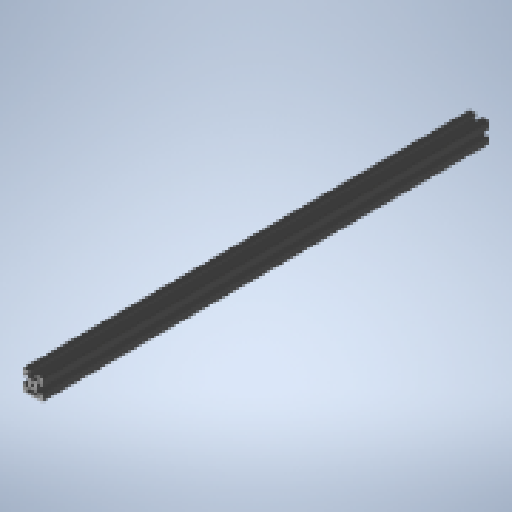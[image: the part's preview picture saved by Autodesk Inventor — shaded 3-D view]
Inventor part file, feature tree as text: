
AUTODESK INVENTOR PART (.ipt)
format: ipt  version: 2024 (Build 280153000, 153)  size: 376,832 bytes
history: native  units: mm
features: other x7, thread x2, sketch x2, extrude x1, hole x1
ambient origin geometry x8: Origin, YZ Plane, XZ Plane, XY Plane, X Axis, Y Axis, Z Axis, Center Point
bodies: Solid1 (feature_tree)
feature tree (13):
  extrude  "Extrusion1"  TaperAngle=0.0deg  [1 undecoded]
  hole  "Hole1"  [1 undecoded]
  other  "C1_XY"
  other  "C1_YZ"
  other  "C1_ZX"
  other  "C1_X"
  other  "C1_Y"
  other  "C1_Z"
  other  "C1_Center"
  thread  "Thread1"  [1 undecoded]
  thread  "Thread2"  [1 undecoded]
  sketch  "Sketch_63"  dims[d2=4.2mm d3=6.0mm d4=4.0mm d5=2.0mm d6=90.0deg d7=440.0mm d8=0.0mm d9=0.0mm d10=10.0mm d11=0.0mm d12=10.0mm d13=0.0mm]
  sketch  "Sketch2"  dims[d0=440.0mm d1=0.0mm]
note: 4 required parameter values undecoded (feature->parameter linkage not recoverable at this tier; creation-order binding heuristic only, values carry confidence <= 0.55)
